# Revit family: Mailboxes_Regency_Outdoor_Parcel_Locker-Salsbury_Industries-Type_II
name_source: partatom
category: Specialty Equipment
revit_build: Autodesk Revit 2016 (Build: 20150714_1515(x64)
units: mm (PartAtom-declared; Revit-internal decimal feet)

## family parameters
Cut with Voids When Loaded = No
Host = Face
OmniClass Number = 23.40.90.14.11
OmniClass Title = Mail Boxes
Part Type = Normal
Room Calculation Point = No
Round Connector Dimension = Use Diameter
Shared = No

## types (1)
- 3304R
    Assembly Code = E1010900
    Assembly Description = Other Commercial Equipment
    Depth = 18.425 "
    Description = 4 Parcel Lockers - Type II - USPS Access
    Door Slot L1 = 3300 Series OPL Parcel Configurations : OPL Parcel Door
    Door Slot L2 = 3300 Series OPL Parcel Configurations : OPL Parcel Door
    Door Slot R1 = 3300 Series OPL Parcel Configurations : OPL Parcel Door
    Door Slot R2 = 3300 Series OPL Parcel Configurations : OPL Parcel Door
    Height = 72.105 "
    Lock Material = Stainless Steel - Salsbury Finish -  Polished
    Manufacturer = Salsbury Industries
    MasterFormat Number = 10 55 26
    MasterFormat Title = Postal Specialties
    Model = 3304R
    OmniClass 23 Number = 23.40.90.14.11
    OmniClass 23 Title = Mail Boxes
    Type Comments = Regency® Decorative Outdoor Parcel Locker (OPL) - Includes Pedestal
    URL = www.mailboxes.com
    Version = 3.0 (02/28/19)
    Width = 31.023 "

## geometry (parser evidence)
native form markers: Blend x4, Sweep x8
no freeform markers — native parametric forms only
